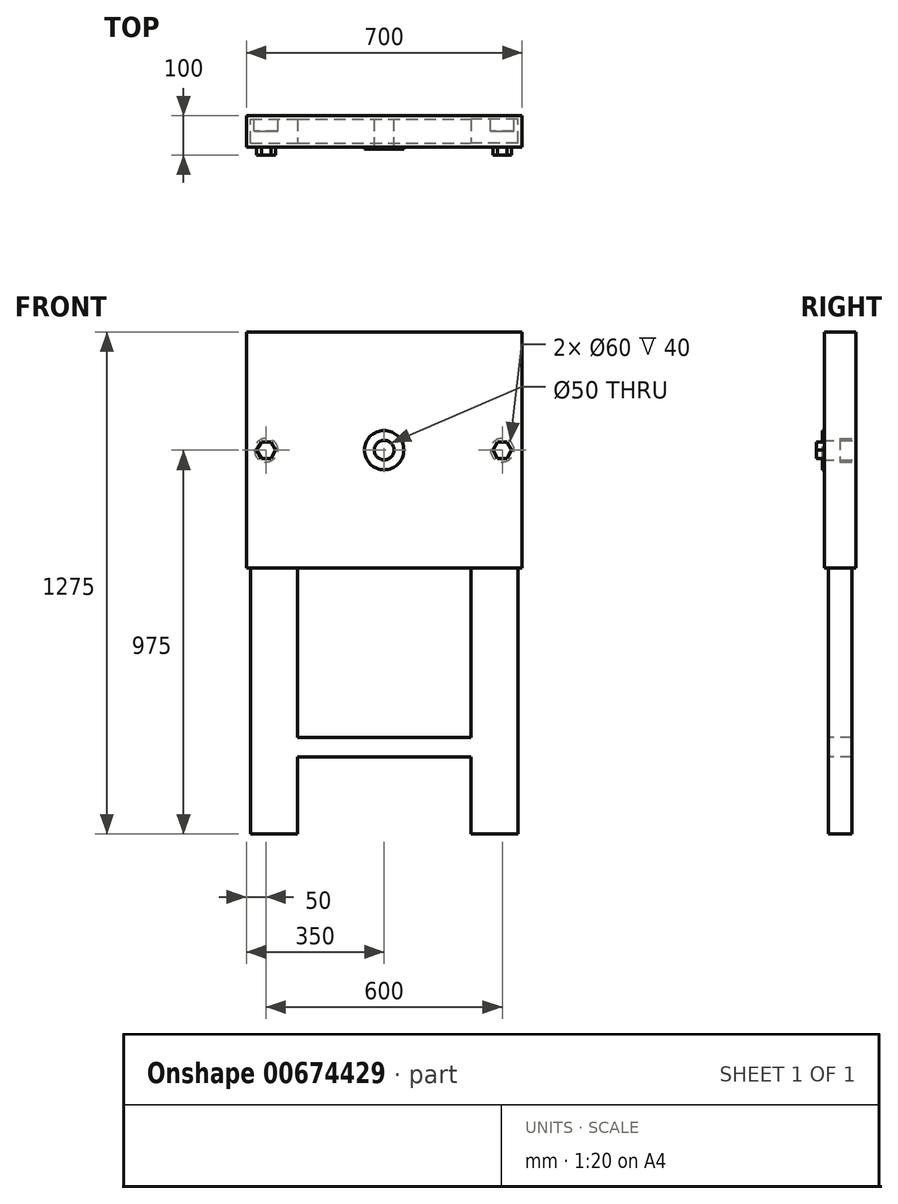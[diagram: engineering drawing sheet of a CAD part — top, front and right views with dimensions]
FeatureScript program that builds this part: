
annotation { "Feature Type Name" : "Feature", "Feature Type Description" : "" }
export const myFeature = defineFeature(function(context is Context, id is Id, definition is map)
    precondition{}
    {
        {
            var Q0;
            Q0=qCreatedBy(makeId("Front.planeOp"),FACE);
            var sketch = newSketch(context, id + "F0", { "sketchPlane" : qUnion([Q0])});
            skLineSegment(sketch, "E0.bottom", {"start": v(350, -300) * mm, "end": v(-350, -300) * mm});
            skLineSegment(sketch, "E0.top", {"start": v(350, 300) * mm, "end": v(-350, 300) * mm});
            skLineSegment(sketch, "E0.left", {"start": v(350, -300) * mm, "end": v(350, 300) * mm});
            skLineSegment(sketch, "E0.right", {"start": v(-350, -300) * mm, "end": v(-350, 300) * mm});
            skPoint(sketch, "E0.middle", {"position": v(0, 0) * mm});
            skCircle(sketch, "E1", {"center": v(0, 0) * mm, "radius": 25 * mm});
            skSolve(sketch);
        }
        {
            var Q0;
            Q0=makeQuery(id+"F0.imprint","IMPRINT",FACE,{"disambiguationData":[TD([[makeQuery(id+"F0.imprint","IMPRINT",EDGE,{"derivedFrom":sQuery(id+"F0.wireOp",EDGE,"E0.bottom")}),-1.0]])]});
            extrude(context, id + "F1", {"entities" : qUnion([Q0]), "endBound" : BoundingType.SYMMETRIC, "depth" : 80 * mm, "offsetDistance" : 25 * mm});
        }
        {
            var Q0;
            Q0=makeQuery(id+"F1.opExtrude","CAP_FACE",FACE,{"disambiguationData":[OSD([sQuery(id+"F0.wireOp",EDGE,"E0.bottom"),sQuery(id+"F0.wireOp",EDGE,"E0.top"),sQuery(id+"F0.wireOp",EDGE,"E0.left"),sQuery(id+"F0.wireOp",EDGE,"E0.right"),sQuery(id+"F0.wireOp",EDGE,"E1")])],"isStart":true});
            var sketch = newSketch(context, id + "F2", { "sketchPlane" : qUnion([Q0])});
            skCircle(sketch, "E2", {"center": v(-300, 0) * mm, "radius": 30 * mm});
            skCircle(sketch, "E3", {"center": v(300, 0) * mm, "radius": 30 * mm});
            skSolve(sketch);
        }
        {
            var Q0;
            Q0 = qSketchRegion(id + "F2", true);
            extrude(context, id + "F3", {"entities" : qUnion([Q0]), "operationType" : NewBodyOperationType.REMOVE, "oppositeDirection" : true, "depth" : 40 * mm, "offsetDistance" : 25 * mm});
        }
        {
            var Q0;
            Q0=makeQuery(id+"F1.opExtrude","CAP_FACE",FACE,{"disambiguationData":[OSD([sQuery(id+"F0.wireOp",EDGE,"E0.bottom"),sQuery(id+"F0.wireOp",EDGE,"E0.top"),sQuery(id+"F0.wireOp",EDGE,"E0.left"),sQuery(id+"F0.wireOp",EDGE,"E0.right"),sQuery(id+"F0.wireOp",EDGE,"E1")])],"isStart":false});
            var sketch = newSketch(context, id + "F4", { "sketchPlane" : qUnion([Q0])});
            skCircle(sketch, "E4.cCircle", {"center": v(-300, 0) * mm, "radius": 20.83 * mm, "construction": true});
            skLineSegment(sketch, "E4.0", {"start": v(-287.97, -20.83) * mm, "end": v(-312.03, -20.83) * mm});
            skLineSegment(sketch, "E4.1", {"start": v(-312.03, -20.83) * mm, "end": v(-324.06, 0) * mm});
            skLineSegment(sketch, "E4.2", {"start": v(-324.06, 0) * mm, "end": v(-312.03, 20.83) * mm});
            skLineSegment(sketch, "E4.3", {"start": v(-312.03, 20.83) * mm, "end": v(-287.97, 20.83) * mm});
            skLineSegment(sketch, "E4.4", {"start": v(-287.97, 20.83) * mm, "end": v(-275.94, 0) * mm});
            skLineSegment(sketch, "E4.5", {"start": v(-275.94, 0) * mm, "end": v(-287.97, -20.83) * mm});
            skPoint(sketch, "E4.0.midPoint", {"position": v(-300, -20.83) * mm});
            skLineSegment(sketch, "E5.MirrorCS", {"start": v(275.94, 0) * mm, "end": v(287.97, -20.83) * mm});
            skLineSegment(sketch, "E6.MirrorCS", {"start": v(312.03, -20.83) * mm, "end": v(324.06, 0) * mm});
            skLineSegment(sketch, "E7.MirrorCS", {"start": v(287.97, 20.83) * mm, "end": v(275.94, 0) * mm});
            skLineSegment(sketch, "E8.MirrorCS", {"start": v(312.03, 20.83) * mm, "end": v(287.97, 20.83) * mm});
            skLineSegment(sketch, "E9.MirrorCS", {"start": v(287.97, -20.83) * mm, "end": v(312.03, -20.83) * mm});
            skLineSegment(sketch, "E10.MirrorCS", {"start": v(324.06, 0) * mm, "end": v(312.03, 20.83) * mm});
            skCircle(sketch, "E11.MirrorC", {"center": v(300, 0) * mm, "radius": 20.83 * mm, "construction": true});
            skPoint(sketch, "E12.MirrorP", {"position": v(300, -20.83) * mm});
            skSolve(sketch);
        }
        {
            var Q0;
            Q0 = qSketchRegion(id + "F4", true);
            extrude(context, id + "F5", {"entities" : qUnion([Q0]), "operationType" : NewBodyOperationType.ADD, "depth" : 20 * mm, "offsetDistance" : 25 * mm});
        }
        {
            var Q0;
            Q0=makeQuery(id+"F1.opExtrude","SWEPT_FACE",FACE,{"disambiguationData":[OSD([sQuery(id+"F0.wireOp",EDGE,"E0.bottom")])]});
            var sketch = newSketch(context, id + "F6", { "sketchPlane" : qUnion([Q0])});
            skLineSegment(sketch, "E13.bottom", {"start": v(-340, 29.4) * mm, "end": v(-220, 29.4) * mm});
            skLineSegment(sketch, "E13.top", {"start": v(-340, -30.6) * mm, "end": v(-220, -30.6) * mm});
            skLineSegment(sketch, "E13.left", {"start": v(-340, 29.4) * mm, "end": v(-340, -30.6) * mm});
            skLineSegment(sketch, "E13.right", {"start": v(-220, 29.4) * mm, "end": v(-220, -30.6) * mm});
            skLineSegment(sketch, "E14.MirrorCS", {"start": v(340, -30.6) * mm, "end": v(220, -30.6) * mm});
            skLineSegment(sketch, "E15.MirrorCS", {"start": v(340, 29.4) * mm, "end": v(220, 29.4) * mm});
            skLineSegment(sketch, "E16.MirrorCS", {"start": v(340, 29.4) * mm, "end": v(340, -30.6) * mm});
            skLineSegment(sketch, "E17.MirrorCS", {"start": v(220, 29.4) * mm, "end": v(220, -30.6) * mm});
            skSolve(sketch);
        }
        {
            var Q0;
            Q0 = qSketchRegion(id + "F6", true);
            extrude(context, id + "F7", {"entities" : qUnion([Q0]), "operationType" : NewBodyOperationType.ADD, "depth" : 675 * mm, "offsetDistance" : 25 * mm});
        }
        {
            var Q0;
            Q0=makeQuery(id+"F7.opExtrude","SWEPT_FACE",FACE,{"disambiguationData":[OSD([sQuery(id+"F6.wireOp",EDGE,"E15.MirrorCS")])]});
            var sketch = newSketch(context, id + "F8", { "sketchPlane" : qUnion([Q0])});
            skLineSegment(sketch, "E18.0", {"start": v(-220, -780) * mm, "end": v(-220, -730) * mm});
            skLineSegment(sketch, "E19.bottom", {"start": v(-220, -730) * mm, "end": v(220, -730) * mm});
            skLineSegment(sketch, "E19.top", {"start": v(-220, -780) * mm, "end": v(220, -780) * mm});
            skLineSegment(sketch, "E19.left", {"start": v(-220, -730) * mm, "end": v(-220, -780) * mm});
            skLineSegment(sketch, "E19.right", {"start": v(220, -730) * mm, "end": v(220, -780) * mm});
            skPoint(sketch, "E20.orphan", {"position": v(-220, -300) * mm});
            skPoint(sketch, "E21.orphan", {"position": v(-220, -975) * mm});
            skSolve(sketch);
        }
        {
            var Q0;
            Q0=makeQuery(id+"F8.imprint","IMPRINT",FACE,{"disambiguationData":[TD([[makeQuery(id+"F8.imprint","IMPRINT",EDGE,{"derivedFrom":sQuery(id+"F8.wireOp",EDGE,"E19.bottom")}),-1.0]])]});
            extrude(context, id + "F9", {"entities" : qUnion([Q0]), "operationType" : NewBodyOperationType.ADD, "oppositeDirection" : true, "depth" : 60 * mm, "offsetDistance" : 25 * mm});
        }
        {
            var Q0;
            Q0=makeQuery(id+"F1.opExtrude","CAP_FACE",FACE,{"disambiguationData":[OSD([sQuery(id+"F0.wireOp",EDGE,"E0.bottom"),sQuery(id+"F0.wireOp",EDGE,"E0.top"),sQuery(id+"F0.wireOp",EDGE,"E0.left"),sQuery(id+"F0.wireOp",EDGE,"E0.right"),sQuery(id+"F0.wireOp",EDGE,"E1")])],"isStart":false});
            var sketch = newSketch(context, id + "F10", { "sketchPlane" : qUnion([Q0])});
            skCircle(sketch, "E22", {"center": v(0, 0) * mm, "radius": 50 * mm});
            skSolve(sketch);
        }
        {
            var Q0;
            Q0=makeQuery(id+"F10.imprint","IMPRINT",FACE,{"disambiguationData":[TD([[makeQuery(id+"F10.imprint","IMPRINT",EDGE,{"derivedFrom":sQuery(id+"F10.wireOp",EDGE,"E22")}),1.0]])]});
            extrude(context, id + "F11", {"entities" : qUnion([Q0]), "operationType" : NewBodyOperationType.ADD, "depth" : 5 * mm, "offsetDistance" : 25 * mm});
        }
    });
